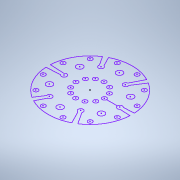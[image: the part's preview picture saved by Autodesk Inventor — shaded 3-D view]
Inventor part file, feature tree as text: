
AUTODESK INVENTOR PART (.ipt)
format: ipt  version: 2021 (Build 250183000, 183)  size: 109,056 bytes
history: native  units: mm
features: sketch x1
ambient origin geometry x8: Origin, YZ Plane, XZ Plane, XY Plane, X Axis, Y Axis, Z Axis, Center Point
feature tree (1):
  sketch  "Sketch1"  dims[d1=60.0deg d2=15.0deg d3=15.0deg d4=62.0mm d7=48.0mm d9=15.0deg d10=23.0mm d12=0.523599mm d13=0.523599mm d14=42.0mm d15=4.0mm]
